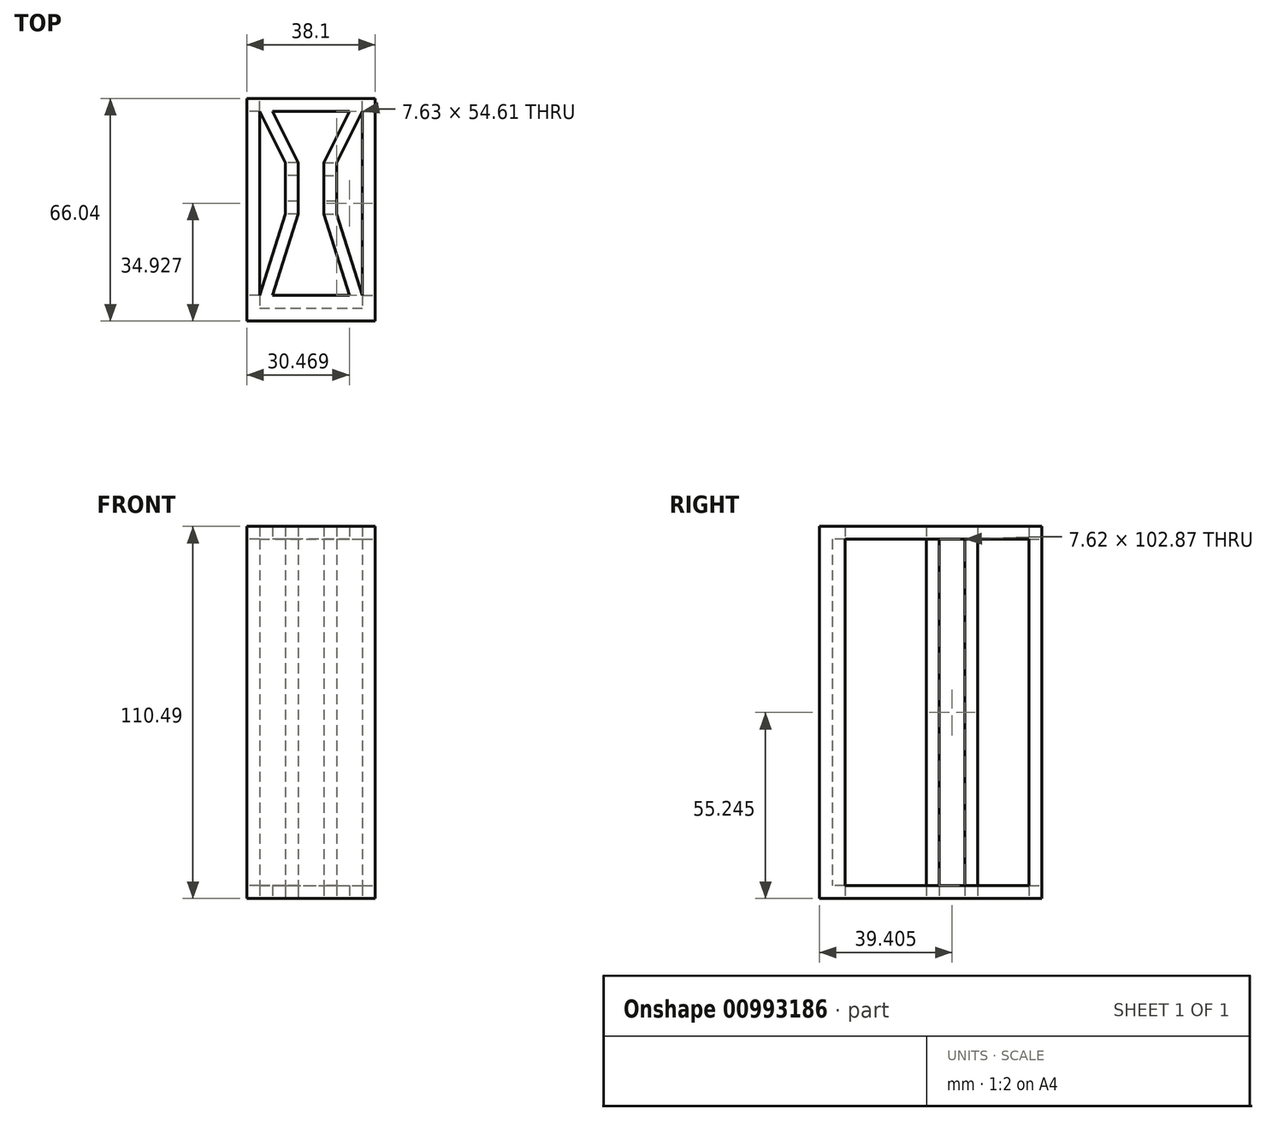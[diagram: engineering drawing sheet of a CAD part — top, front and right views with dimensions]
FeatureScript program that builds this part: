
annotation { "Feature Type Name" : "Feature", "Feature Type Description" : "" }
export const myFeature = defineFeature(function(context is Context, id is Id, definition is map)
    precondition{}
    {
        {
            var Q0;
            Q0=qCreatedBy(makeId("Top.planeOp"),FACE);
            var sketch = newSketch(context, id + "F0", { "sketchPlane" : qUnion([Q0])});
            skLineSegment(sketch, "E0.bottom", {"start": v(-48.05, 33.62) * mm, "end": v(-9.95, 33.62) * mm});
            skLineSegment(sketch, "E0.top", {"start": v(-48.05, -28.6) * mm, "end": v(-9.95, -28.6) * mm});
            skLineSegment(sketch, "E0.left", {"start": v(-48.05, 33.62) * mm, "end": v(-48.05, -28.6) * mm});
            skLineSegment(sketch, "E0.right", {"start": v(-9.95, 33.62) * mm, "end": v(-9.95, -28.6) * mm});
            skLineSegment(sketch, "E1.bottom", {"start": v(-44.24, 29.81) * mm, "end": v(-13.76, 29.81) * mm});
            skLineSegment(sketch, "E1.top", {"start": v(-44.24, -24.8) * mm, "end": v(-13.76, -24.8) * mm});
            skLineSegment(sketch, "E1.left", {"start": v(-44.24, 29.81) * mm, "end": v(-44.24, -24.8) * mm});
            skLineSegment(sketch, "E1.right", {"start": v(-13.76, 29.81) * mm, "end": v(-13.76, -24.8) * mm});
            skPoint(sketch, "E2.middle", {"position": v(-29, 5.08) * mm});
            skPoint(sketch, "E2.middle.positionSnap0", {"position": v(-29, 29.81) * mm});
            skPoint(sketch, "E2.centerSnap0", {"position": v(-29, 29.81) * mm});
            skPoint(sketch, "E3.endSnap0", {"position": v(-25.2, 5.08) * mm});
            skLineSegment(sketch, "E4.left", {"start": v(-32.81, 10.8) * mm, "end": v(-32.81, 14.6) * mm});
            skLineSegment(sketch, "E5.bottom", {"start": v(-25.2, 10.8) * mm, "end": v(-21.4, 10.8) * mm});
            skLineSegment(sketch, "E5.top", {"start": v(-25.2, 14.6) * mm, "end": v(-21.4, 14.6) * mm});
            skLineSegment(sketch, "E5.left", {"start": v(-25.2, 10.8) * mm, "end": v(-25.2, 14.6) * mm});
            skLineSegment(sketch, "E5.right", {"start": v(-21.4, 10.8) * mm, "end": v(-21.4, 14.6) * mm});
            skLineSegment(sketch, "E6.left", {"start": v(-25.2, 3.17) * mm, "end": v(-25.2, 0.58) * mm});
            skLineSegment(sketch, "E7.bottom", {"start": v(-32.81, 14.6) * mm, "end": v(-36.61, 14.6) * mm});
            skLineSegment(sketch, "E7.top", {"start": v(-32.81, 10.79) * mm, "end": v(-36.61, 10.79) * mm});
            skLineSegment(sketch, "E7.left", {"start": v(-32.81, 14.6) * mm, "end": v(-32.81, 10.79) * mm});
            skLineSegment(sketch, "E7.right", {"start": v(-36.61, 14.6) * mm, "end": v(-36.61, 10.79) * mm});
            skLineSegment(sketch, "E8", {"start": v(-44.24, 29.81) * mm, "end": v(-36.61, 14.6) * mm});
            skLineSegment(sketch, "E9", {"start": v(-32.81, 14.6) * mm, "end": v(-40.45, 29.81) * mm});
            skLineSegment(sketch, "E10", {"start": v(-21.4, 14.6) * mm, "end": v(-13.76, 29.81) * mm});
            skLineSegment(sketch, "E11", {"start": v(-25.2, 14.6) * mm, "end": v(-17.56, 29.81) * mm});
            skLineSegment(sketch, "E12.bottom", {"start": v(-32.81, 3.17) * mm, "end": v(-36.61, 3.17) * mm});
            skLineSegment(sketch, "E12.top", {"start": v(-32.81, -0.63) * mm, "end": v(-36.61, -0.63) * mm});
            skLineSegment(sketch, "E12.left", {"start": v(-32.81, 3.17) * mm, "end": v(-32.81, -0.63) * mm});
            skLineSegment(sketch, "E12.right", {"start": v(-36.61, 3.17) * mm, "end": v(-36.61, -0.63) * mm});
            skLineSegment(sketch, "E13.top", {"start": v(-21.4, 3.17) * mm, "end": v(-25.2, 3.17) * mm});
            skLineSegment(sketch, "E14", {"start": v(-25.2, -0.63) * mm, "end": v(-21.4, -0.63) * mm});
            skLineSegment(sketch, "E15", {"start": v(-21.4, -0.63) * mm, "end": v(-21.4, 3.17) * mm});
            skLineSegment(sketch, "E16", {"start": v(-25.2, 3.17) * mm, "end": v(-25.2, -0.63) * mm});
            skLineSegment(sketch, "E17", {"start": v(-36.61, -0.63) * mm, "end": v(-44.24, -24.8) * mm});
            skLineSegment(sketch, "E18", {"start": v(-32.81, -0.63) * mm, "end": v(-40.43, -24.8) * mm});
            skLineSegment(sketch, "E19", {"start": v(-21.4, -0.63) * mm, "end": v(-13.76, -24.8) * mm});
            skLineSegment(sketch, "E20", {"start": v(-25.2, -0.63) * mm, "end": v(-17.57, -24.8) * mm});
            skLineSegment(sketch, "E21.bottom", {"start": v(-36.61, 10.79) * mm, "end": v(-32.81, 10.79) * mm});
            skLineSegment(sketch, "E21.top", {"start": v(-36.61, 3.17) * mm, "end": v(-32.81, 3.17) * mm});
            skLineSegment(sketch, "E21.left", {"start": v(-36.61, 10.79) * mm, "end": v(-36.61, 3.17) * mm});
            skLineSegment(sketch, "E21.right", {"start": v(-32.81, 10.79) * mm, "end": v(-32.81, 3.17) * mm});
            skLineSegment(sketch, "E22.top", {"start": v(-25.2, 3.17) * mm, "end": v(-21.4, 3.17) * mm});
            skLineSegment(sketch, "E22.left", {"start": v(-25.2, 10.8) * mm, "end": v(-25.2, 3.17) * mm});
            skLineSegment(sketch, "E22.right", {"start": v(-21.4, 10.8) * mm, "end": v(-21.4, 3.17) * mm});
            skSolve(sketch);
        }
        {
            var Q0;
            Q0=makeQuery(id+"F0.imprint","IMPRINT",FACE,{"disambiguationData":[TD([[makeQuery(id+"F0.imprint","IMPRINT",EDGE,{"derivedFrom":sQuery(id+"F0.wireOp",EDGE,"E7.bottom")}),-1.0]])]});
            var Q1;
            Q1=makeQuery(id+"F0.imprint","IMPRINT",FACE,{"disambiguationData":[TD([[makeQuery(id+"F0.imprint","IMPRINT",EDGE,{"derivedFrom":sQuery(id+"F0.wireOp",EDGE,"E0.bottom")}),-1.0]])]});
            var Q2;
            Q2=makeQuery(id+"F0.imprint","IMPRINT",FACE,{"disambiguationData":[TD([[makeQuery(id+"F0.imprint","IMPRINT",EDGE,{"derivedFrom":sQuery(id+"F0.wireOp",EDGE,"E5.top")}),1.0]])]});
            var Q3;
            Q3=makeQuery(id+"F0.imprint","IMPRINT",FACE,{"disambiguationData":[TD([[makeQuery(id+"F0.imprint","IMPRINT",EDGE,{"derivedFrom":sQuery(id+"F0.wireOp",EDGE,"E12.top")}),1.0]])]});
            var Q4;
            Q4=makeQuery(id+"F0.imprint","IMPRINT",FACE,{"disambiguationData":[TD([[makeQuery(id+"F0.imprint","IMPRINT",EDGE,{"derivedFrom":sQuery(id+"F0.wireOp",EDGE,"E14")}),-1.0]])]});
            var Q5;
            Q5=makeQuery(id+"F0.imprint","IMPRINT",FACE,{"disambiguationData":[TD([[makeQuery(id+"F0.imprint","IMPRINT",EDGE,{"derivedFrom":sQuery(id+"F0.wireOp",EDGE,"E21.bottom")}),-1.0]])]});
            var Q6;
            Q6=makeQuery(id+"F0.imprint","IMPRINT",FACE,{"disambiguationData":[TD([[makeQuery(id+"F0.imprint","IMPRINT",EDGE,{"derivedFrom":sQuery(id+"F0.wireOp",EDGE,"E5.bottom")}),-1.0]])]});
            var Q7;
            {var subQ3=sQuery(id+"F0.wireOp",EDGE,"E7.bottom");Q7=makeQuery(id+"F0.imprint","IMPRINT",FACE,{"disambiguationData":[TD([[makeQuery(id+"F0.imprint","IMPRINT",EDGE,{"derivedFrom":subQ3}),1.0]])]});}
            var Q8;
            Q8=makeQuery(id+"F0.imprint","IMPRINT",FACE,{"disambiguationData":[TD([[makeQuery(id+"F0.imprint","IMPRINT",EDGE,{"derivedFrom":sQuery(id+"F0.wireOp",EDGE,"E12.bottom")}),1.0]])]});
            var Q9;
            Q9=makeQuery(id+"F0.imprint","IMPRINT",FACE,{"disambiguationData":[TD([[makeQuery(id+"F0.imprint","IMPRINT",EDGE,{"derivedFrom":sQuery(id+"F0.wireOp",EDGE,"E5.top")}),-1.0]])]});
            var Q10;
            {var subQ1=sQuery(id+"F0.wireOp",EDGE,"E14");Q10=makeQuery(id+"F0.imprint","IMPRINT",FACE,{"disambiguationData":[TD([[makeQuery(id+"F0.imprint","IMPRINT",EDGE,{"derivedFrom":subQ1}),1.0]])]});}
            extrude(context, id + "F1", {"entities" : qUnion([Q0, Q1, Q2, Q3, Q4, Q5, Q6, Q7, Q8, Q9, Q10]), "depth" : 3.8 * mm, "offsetDistance" : 25.4 * mm});
        }
        {
            var Q0;
            {var subQ3=sQuery(id+"F0.wireOp",EDGE,"E7.bottom");Q0=makeQuery(id+"F0.imprint","IMPRINT",FACE,{"disambiguationData":[TD([[makeQuery(id+"F0.imprint","IMPRINT",EDGE,{"derivedFrom":subQ3}),1.0]])]});}
            var Q1;
            Q1=makeQuery(id+"F0.imprint","IMPRINT",FACE,{"disambiguationData":[TD([[makeQuery(id+"F0.imprint","IMPRINT",EDGE,{"derivedFrom":sQuery(id+"F0.wireOp",EDGE,"E12.bottom")}),1.0]])]});
            var Q2;
            {var subQ1=sQuery(id+"F0.wireOp",EDGE,"E13.top");Q2=makeQuery(id+"F0.imprint","IMPRINT",FACE,{"disambiguationData":[TD([[makeQuery(id+"F0.imprint","IMPRINT",EDGE,{"derivedFrom":subQ1}),1.0]])]});}
            var Q3;
            Q3=makeQuery(id+"F0.imprint","IMPRINT",FACE,{"disambiguationData":[TD([[makeQuery(id+"F0.imprint","IMPRINT",EDGE,{"derivedFrom":sQuery(id+"F0.wireOp",EDGE,"E5.bottom")}),1.0]])]});
            var Q4;
            Q4=makeQuery(id+"F0.imprint","IMPRINT",FACE,{"disambiguationData":[TD([[makeQuery(id+"F0.imprint","IMPRINT",EDGE,{"derivedFrom":sQuery(id+"F0.wireOp",EDGE,"E5.top")}),-1.0]])]});
            var Q5;
            {var subQ1=sQuery(id+"F0.wireOp",EDGE,"E14");Q5=makeQuery(id+"F0.imprint","IMPRINT",FACE,{"disambiguationData":[TD([[makeQuery(id+"F0.imprint","IMPRINT",EDGE,{"derivedFrom":subQ1}),1.0]])]});}
            extrude(context, id + "F2", {"entities" : qUnion([Q0, Q1, Q2, Q3, Q4, Q5]), "operationType" : NewBodyOperationType.ADD, "depth" : 106.68 * mm, "offsetDistance" : 25.4 * mm});
        }
        {
            var Q0;
            Q0=makeQuery(id+"F1.opExtrude","CAP_FACE",FACE,{"disambiguationData":[OSD([sQuery(id+"F0.wireOp",EDGE,"E0.bottom"),sQuery(id+"F0.wireOp",EDGE,"E0.top"),sQuery(id+"F0.wireOp",EDGE,"E0.left"),sQuery(id+"F0.wireOp",EDGE,"E0.right"),sQuery(id+"F0.wireOp",EDGE,"E1.bottom"),sQuery(id+"F0.wireOp",EDGE,"E1.top"),sQuery(id+"F0.wireOp",EDGE,"E1.left"),sQuery(id+"F0.wireOp",EDGE,"E1.right"),sQuery(id+"F0.wireOp",EDGE,"E5.top"),sQuery(id+"F0.wireOp",EDGE,"E7.bottom"),sQuery(id+"F0.wireOp",EDGE,"E8"),sQuery(id+"F0.wireOp",EDGE,"E9"),sQuery(id+"F0.wireOp",EDGE,"E10"),sQuery(id+"F0.wireOp",EDGE,"E11"),sQuery(id+"F0.wireOp",EDGE,"E12.top"),sQuery(id+"F0.wireOp",EDGE,"E14"),sQuery(id+"F0.wireOp",EDGE,"E17"),sQuery(id+"F0.wireOp",EDGE,"E18"),sQuery(id+"F0.wireOp",EDGE,"E19"),sQuery(id+"F0.wireOp",EDGE,"E20")])],"isStart":false});
            var sketch = newSketch(context, id + "F3", { "sketchPlane" : qUnion([Q0])});
            skLineSegment(sketch, "E23.bottom", {"start": v(-44.24, 29.81) * mm, "end": v(-48.05, 29.81) * mm});
            skLineSegment(sketch, "E23.top", {"start": v(-44.24, 33.62) * mm, "end": v(-48.05, 33.62) * mm});
            skLineSegment(sketch, "E23.left", {"start": v(-44.24, 29.81) * mm, "end": v(-44.24, 33.62) * mm});
            skLineSegment(sketch, "E23.right", {"start": v(-48.05, 29.81) * mm, "end": v(-48.05, 33.62) * mm});
            skLineSegment(sketch, "E24.bottom", {"start": v(-13.76, 29.81) * mm, "end": v(-9.95, 29.81) * mm});
            skLineSegment(sketch, "E24.top", {"start": v(-13.76, 33.62) * mm, "end": v(-9.95, 33.62) * mm});
            skLineSegment(sketch, "E24.left", {"start": v(-13.76, 29.81) * mm, "end": v(-13.76, 33.62) * mm});
            skLineSegment(sketch, "E24.right", {"start": v(-9.95, 29.81) * mm, "end": v(-9.95, 33.62) * mm});
            skLineSegment(sketch, "E25.bottom", {"start": v(-44.24, -24.8) * mm, "end": v(-48.05, -24.8) * mm});
            skLineSegment(sketch, "E25.top", {"start": v(-44.24, -28.6) * mm, "end": v(-48.05, -28.6) * mm});
            skLineSegment(sketch, "E25.left", {"start": v(-44.24, -24.8) * mm, "end": v(-44.24, -28.6) * mm});
            skLineSegment(sketch, "E25.right", {"start": v(-48.05, -24.8) * mm, "end": v(-48.05, -28.6) * mm});
            skLineSegment(sketch, "E26.bottom", {"start": v(-13.76, -24.8) * mm, "end": v(-9.95, -24.8) * mm});
            skLineSegment(sketch, "E26.top", {"start": v(-13.76, -28.6) * mm, "end": v(-9.95, -28.6) * mm});
            skLineSegment(sketch, "E26.left", {"start": v(-13.76, -24.8) * mm, "end": v(-13.76, -28.6) * mm});
            skLineSegment(sketch, "E26.right", {"start": v(-9.95, -24.8) * mm, "end": v(-9.95, -28.6) * mm});
            skSolve(sketch);
        }
        {
            var Q0;
            Q0=makeQuery(id+"F3.imprint","IMPRINT",FACE,{"disambiguationData":[TD([[makeQuery(id+"F3.imprint","IMPRINT",EDGE,{"derivedFrom":sQuery(id+"F3.wireOp",EDGE,"E23.bottom")}),-1.0]])]});
            var Q1;
            Q1=makeQuery(id+"F3.imprint","IMPRINT",FACE,{"disambiguationData":[TD([[makeQuery(id+"F3.imprint","IMPRINT",EDGE,{"derivedFrom":sQuery(id+"F3.wireOp",EDGE,"E24.bottom")}),1.0]])]});
            var Q2;
            Q2=makeQuery(id+"F3.imprint","IMPRINT",FACE,{"disambiguationData":[TD([[makeQuery(id+"F3.imprint","IMPRINT",EDGE,{"derivedFrom":sQuery(id+"F3.wireOp",EDGE,"E25.bottom")}),1.0]])]});
            var Q3;
            Q3=makeQuery(id+"F3.imprint","IMPRINT",FACE,{"disambiguationData":[TD([[makeQuery(id+"F3.imprint","IMPRINT",EDGE,{"derivedFrom":sQuery(id+"F3.wireOp",EDGE,"E26.bottom")}),-1.0]])]});
            extrude(context, id + "F4", {"entities" : qUnion([Q0, Q1, Q2, Q3]), "operationType" : NewBodyOperationType.ADD, "depth" : 102.87 * mm, "offsetDistance" : 25.4 * mm});
        }
        {
            var Q0;
            Q0=makeQuery(id+"F4.opExtrude","CAP_FACE",FACE,{"disambiguationData":[OSD([sQuery(id+"F3.wireOp",EDGE,"E23.bottom"),sQuery(id+"F3.wireOp",EDGE,"E23.top"),sQuery(id+"F3.wireOp",EDGE,"E23.left"),sQuery(id+"F3.wireOp",EDGE,"E23.right")])],"isStart":false});
            var sketch = newSketch(context, id + "F5", { "sketchPlane" : qUnion([Q0])});
            skLineSegment(sketch, "E27.bottom", {"start": v(-48.05, 33.62) * mm, "end": v(-9.96, 33.62) * mm});
            skLineSegment(sketch, "E27.top", {"start": v(-48.05, -28.62) * mm, "end": v(-9.96, -28.62) * mm});
            skLineSegment(sketch, "E27.left", {"start": v(-48.05, 33.62) * mm, "end": v(-48.05, -28.62) * mm});
            skLineSegment(sketch, "E27.right", {"start": v(-9.96, 33.62) * mm, "end": v(-9.96, -28.62) * mm});
            skSolve(sketch);
        }
        {
            var Q0;
            Q0 = qSketchRegion(id + "F5", true);
            extrude(context, id + "F6", {"entities" : qUnion([Q0]), "operationType" : NewBodyOperationType.ADD, "depth" : 3.8 * mm, "offsetDistance" : 25.4 * mm});
        }
        {
            var Q0;
            Q0=makeQuery(id+"F6.opExtrude","CAP_FACE",FACE,{"disambiguationData":[OSD([sQuery(id+"F5.wireOp",EDGE,"E27.bottom"),sQuery(id+"F5.wireOp",EDGE,"E27.top"),sQuery(id+"F5.wireOp",EDGE,"E27.left"),sQuery(id+"F5.wireOp",EDGE,"E27.right")])],"isStart":true});
            var sketch = newSketch(context, id + "F7", { "sketchPlane" : qUnion([Q0])});
            skLineSegment(sketch, "E28", {"start": v(-21.4, -14.6) * mm, "end": v(-13.76, -29.81) * mm});
            skLineSegment(sketch, "E29", {"start": v(-13.76, -29.81) * mm, "end": v(-44.24, -29.81) * mm});
            skLineSegment(sketch, "E30", {"start": v(-44.24, -29.81) * mm, "end": v(-36.61, -14.6) * mm});
            skLineSegment(sketch, "E31", {"start": v(-21.4, -10.8) * mm, "end": v(-21.4, -3.17) * mm});
            skLineSegment(sketch, "E32", {"start": v(-21.4, 0.63) * mm, "end": v(-13.76, 24.8) * mm});
            skLineSegment(sketch, "E33", {"start": v(-13.76, 24.8) * mm, "end": v(-44.24, 24.8) * mm});
            skLineSegment(sketch, "E34", {"start": v(-44.24, 24.8) * mm, "end": v(-36.61, 0.63) * mm});
            skLineSegment(sketch, "E35", {"start": v(-36.61, 0.63) * mm, "end": v(-36.61, -10.79) * mm});
            skLineSegment(sketch, "E36.left", {"start": v(-25.2, -10.8) * mm, "end": v(-25.2, -3.17) * mm});
            skLineSegment(sketch, "E36.right", {"start": v(-32.81, -10.8) * mm, "end": v(-32.81, -3.17) * mm});
            skLineSegment(sketch, "E37", {"start": v(-25.2, -14.6) * mm, "end": v(-17.56, -29.81) * mm});
            skLineSegment(sketch, "E38", {"start": v(-32.81, -14.6) * mm, "end": v(-40.45, -29.81) * mm});
            skLineSegment(sketch, "E39", {"start": v(-25.2, 0.63) * mm, "end": v(-17.58, 24.8) * mm});
            skPoint(sketch, "E39.endSnap0", {"position": v(-17.58, 12.72) * mm});
            skLineSegment(sketch, "E40", {"start": v(-32.81, 0.63) * mm, "end": v(-40.45, 24.8) * mm});
            skLineSegment(sketch, "E41", {"start": v(-13.76, -29.81) * mm, "end": v(-13.76, 24.8) * mm});
            skLineSegment(sketch, "E42", {"start": v(-44.24, -29.81) * mm, "end": v(-44.24, 24.8) * mm});
            skSolve(sketch);
        }
        {
            var Q0;
            Q0=makeQuery(id+"F7.imprint","IMPRINT",FACE,{"disambiguationData":[TD([[makeQuery(id+"F7.imprint","IMPRINT",EDGE,{"derivedFrom":sQuery(id+"F7.wireOp",EDGE,"E36.left")}),1.0]])]});
            var Q1;
            Q1=makeQuery(id+"F7.imprint","IMPRINT",FACE,{"disambiguationData":[TD([[makeQuery(id+"F7.imprint","IMPRINT",EDGE,{"derivedFrom":sQuery(id+"F7.wireOp",EDGE,"E28")}),1.0]])]});
            var Q2;
            Q2=makeQuery(id+"F7.imprint","IMPRINT",FACE,{"disambiguationData":[TD([[makeQuery(id+"F7.imprint","IMPRINT",EDGE,{"derivedFrom":sQuery(id+"F7.wireOp",EDGE,"E30")}),1.0]])]});
            extrude(context, id + "F8", {"entities" : qUnion([Q0, Q1, Q2]), "operationType" : NewBodyOperationType.REMOVE, "oppositeDirection" : true, "depth" : 25.4 * mm, "offsetDistance" : 25.4 * mm});
        }
        {
            var Q0;
            Q0=makeQuery(id+"F4.boolean.opBoolean","MERGE",FACE,{"derivedFrom":[makeQuery(id+"F1.opExtrude","SWEPT_FACE",FACE,{"disambiguationData":[OSD([sQuery(id+"F0.wireOp",EDGE,"E0.top")])]}),makeQuery(id+"F4.opExtrude","SWEPT_FACE",FACE,{"disambiguationData":[OSD([sQuery(id+"F3.wireOp",EDGE,"E25.top")])]}),makeQuery(id+"F4.opExtrude","SWEPT_FACE",FACE,{"disambiguationData":[OSD([sQuery(id+"F3.wireOp",EDGE,"E26.top")])]})]});
            var sketch = newSketch(context, id + "F9", { "sketchPlane" : qUnion([Q0])});
            skLineSegment(sketch, "E43.bottom", {"start": v(-9.95, 0) * mm, "end": v(-48.05, 0) * mm});
            skLineSegment(sketch, "E43.top", {"start": v(-9.95, 110.5) * mm, "end": v(-48.05, 110.5) * mm});
            skLineSegment(sketch, "E43.left", {"start": v(-9.95, 0) * mm, "end": v(-9.95, 110.5) * mm});
            skLineSegment(sketch, "E43.right", {"start": v(-48.05, 0) * mm, "end": v(-48.05, 110.5) * mm});
            skSolve(sketch);
        }
        {
            var Q0;
            {var subQ3=sQuery(id+"F9.wireOp",EDGE,"E43.top");Q0=makeQuery(id+"F9.imprint","IMPRINT",FACE,{"disambiguationData":[TD([[makeQuery(id+"F9.imprint","IMPRINT",EDGE,{"derivedFrom":subQ3}),1.0]])]});}
            var Q1;
            {var subQ3=sQuery(id+"F9.wireOp",EDGE,"E43.bottom");Q1=makeQuery(id+"F9.imprint","IMPRINT",FACE,{"disambiguationData":[TD([[makeQuery(id+"F9.imprint","IMPRINT",EDGE,{"derivedFrom":subQ3}),1.0]])]});}
            extrude(context, id + "F10", {"entities" : qUnion([Q0, Q1]), "operationType" : NewBodyOperationType.ADD, "depth" : 3.8 * mm, "offsetDistance" : 25.4 * mm});
        }
    });
